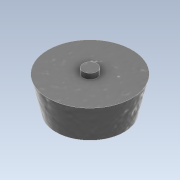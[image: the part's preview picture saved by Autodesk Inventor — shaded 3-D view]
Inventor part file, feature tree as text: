
AUTODESK INVENTOR PART (.ipt)
format: ipt  version: 2022 (Build 260153000, 153)  size: 95,232 bytes
history: native  units: mm
features: sketch x2, revolve x1, extrude x1
ambient origin geometry x8: Origin, YZ Plane, XZ Plane, XY Plane, X Axis, Y Axis, Z Axis, Center Point
bodies: Solid1 (feature_tree)
feature tree (4):
  revolve  "Revolution1"  Angle=90.0deg
  extrude  "Extrusion1"  Depth=2.0mm TaperAngle=0.0deg
  sketch  "Sketch1"  dims[d0=15.0mm d1=90.0deg]
  sketch  "Sketch2"  dims[d2=5.0mm d3=2.0mm d4=0.0mm]
